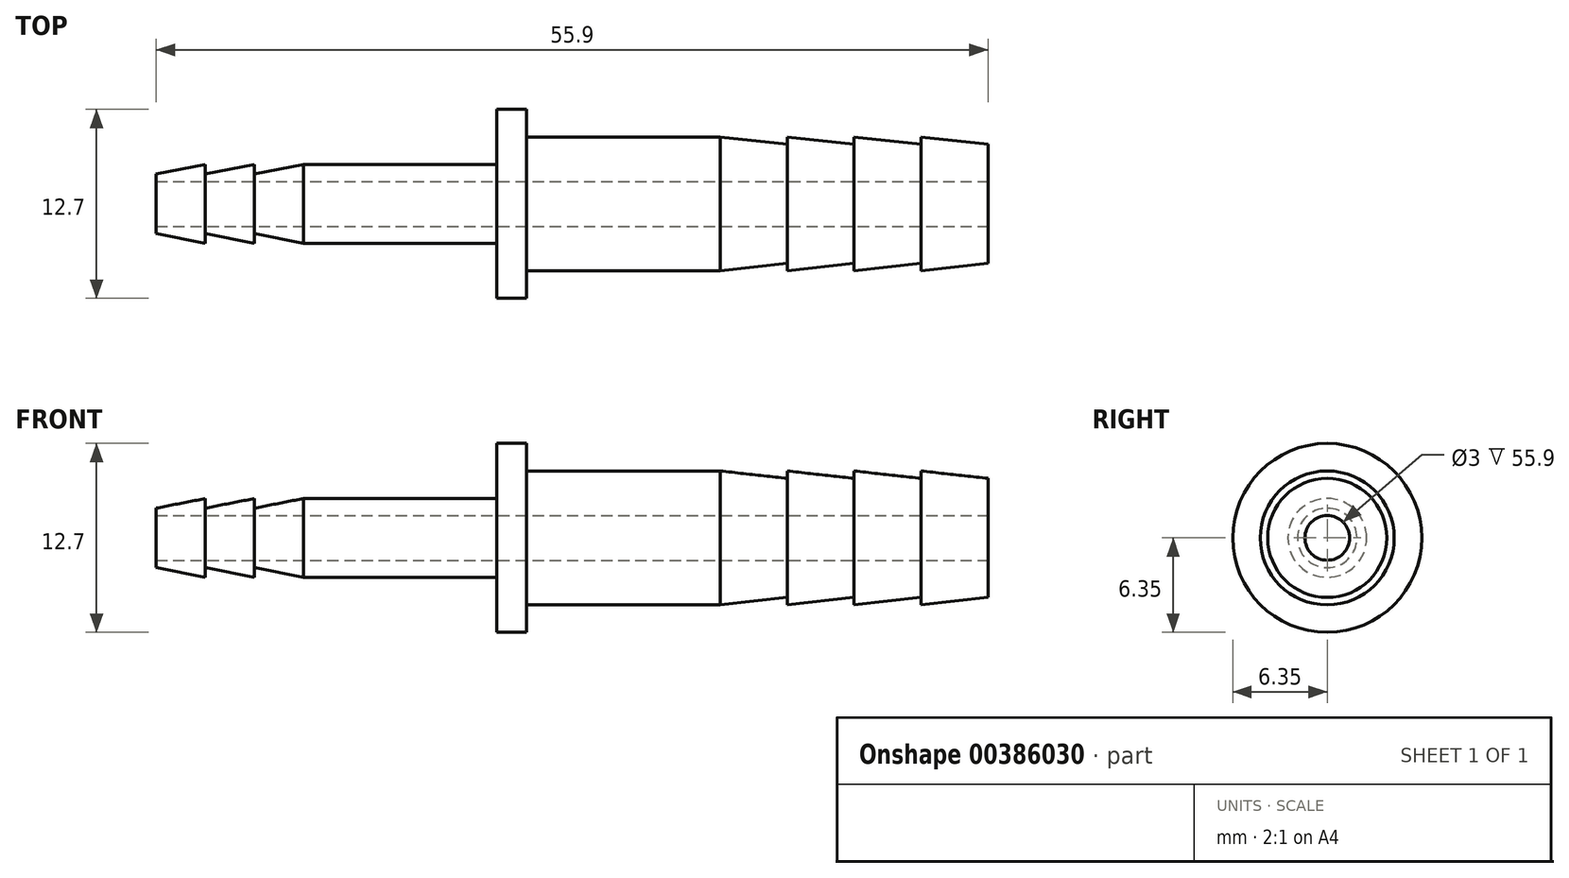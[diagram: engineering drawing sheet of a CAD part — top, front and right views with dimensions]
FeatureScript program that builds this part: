
annotation { "Feature Type Name" : "Feature", "Feature Type Description" : "" }
export const myFeature = defineFeature(function(context is Context, id is Id, definition is map)
    precondition{}
    {
        {
            var Q0;
            Q0=qCreatedBy(makeId("Front.planeOp"),FACE);
            var sketch = newSketch(context, id + "F0", { "sketchPlane" : qUnion([Q0])});
            skLineSegment(sketch, "E0.bottom", {"start": v(14, 4.5) * mm, "end": v(1, 4.5) * mm});
            skLineSegment(sketch, "E1", {"start": v(18.5, 4) * mm, "end": v(14, 4.5) * mm});
            skLineSegment(sketch, "E2", {"start": v(23, 4) * mm, "end": v(18.5, 4.5) * mm});
            skLineSegment(sketch, "E3", {"start": v(27.5, 4) * mm, "end": v(23, 4.5) * mm});
            skLineSegment(sketch, "E4.top", {"start": v(-14, 2.65) * mm, "end": v(-1, 2.65) * mm});
            skLineSegment(sketch, "E5", {"start": v(-17.3, 0) * mm, "end": v(-17.3, 2) * mm});
            skLineSegment(sketch, "E6", {"start": v(-17.3, 2) * mm, "end": v(-14, 2.65) * mm});
            skLineSegment(sketch, "E7", {"start": v(-20.6, 0) * mm, "end": v(-20.6, 2) * mm});
            skLineSegment(sketch, "E8", {"start": v(-20.6, 2) * mm, "end": v(-17.3, 2.65) * mm});
            skLineSegment(sketch, "E9", {"start": v(-23.9, 0) * mm, "end": v(-23.9, 2) * mm});
            skLineSegment(sketch, "E10", {"start": v(-23.9, 2) * mm, "end": v(-20.6, 2.65) * mm});
            skLineSegment(sketch, "E11", {"start": v(32, 4) * mm, "end": v(27.5, 4.5) * mm});
            skLineSegment(sketch, "E12.trimOffspring", {"start": v(-17.3, 2) * mm, "end": v(-17.3, 2.65) * mm});
            skLineSegment(sketch, "E13.trimOffspring", {"start": v(-20.6, 2) * mm, "end": v(-20.6, 2.65) * mm});
            skLineSegment(sketch, "E14", {"start": v(23, 4.5) * mm, "end": v(23, 4) * mm});
            skLineSegment(sketch, "E15", {"start": v(32, 4) * mm, "end": v(32, 0) * mm});
            skLineSegment(sketch, "E16", {"start": v(-23.9, 0) * mm, "end": v(32, 0) * mm});
            skLineSegment(sketch, "E17.bottom", {"start": v(1, 6.35) * mm, "end": v(-1, 6.35) * mm});
            skLineSegment(sketch, "E17.left", {"start": v(1, 6.35) * mm, "end": v(1, 4.5) * mm});
            skLineSegment(sketch, "E17.right", {"start": v(-1, 6.35) * mm, "end": v(-1, 2.65) * mm});
            skPoint(sketch, "E17.middle", {"position": v(0, 0) * mm});
            skLineSegment(sketch, "E18", {"start": v(27.5, 4) * mm, "end": v(27.5, 4.5) * mm});
            skLineSegment(sketch, "E19", {"start": v(18.5, 4) * mm, "end": v(18.5, 4.5) * mm});
            skLineSegment(sketch, "E20", {"start": v(-12.64, 18.93) * mm, "end": v(-12.64, 14.43) * mm});
            skLineSegment(sketch, "E21.top", {"start": v(-17.64, 17.08) * mm, "end": v(-12.64, 17.08) * mm});
            skLineSegment(sketch, "E22", {"start": v(-20.94, 14.43) * mm, "end": v(-20.94, 16.43) * mm});
            skLineSegment(sketch, "E23", {"start": v(-20.94, 16.43) * mm, "end": v(-17.64, 17.08) * mm});
            skLineSegment(sketch, "E24", {"start": v(-24.24, 14.43) * mm, "end": v(-24.24, 16.43) * mm});
            skLineSegment(sketch, "E25", {"start": v(-24.24, 16.43) * mm, "end": v(-20.94, 17.08) * mm});
            skLineSegment(sketch, "E26", {"start": v(-27.54, 14.43) * mm, "end": v(-27.54, 16.43) * mm});
            skLineSegment(sketch, "E27", {"start": v(-27.54, 16.43) * mm, "end": v(-24.24, 17.08) * mm});
            skLineSegment(sketch, "E28.trimOffspring", {"start": v(-20.94, 16.43) * mm, "end": v(-20.94, 17.08) * mm});
            skLineSegment(sketch, "E29.trimOffspring", {"start": v(-24.24, 16.43) * mm, "end": v(-24.24, 17.08) * mm});
            skLineSegment(sketch, "E30.trimOffspring", {"start": v(-12.64, 14.43) * mm, "end": v(-12.64, 18.93) * mm});
            skPoint(sketch, "E31.middle", {"position": v(-12.64, 14.43) * mm});
            skPoint(sketch, "E17.top.end.orphan", {"position": v(-1, -6.35) * mm});
            skPoint(sketch, "E17.top.start.orphan", {"position": v(1, -6.35) * mm});
            skSolve(sketch);
        }
        {
            var Q0;
            {var subQ1=sQuery(id+"F0.wireOp",EDGE,"E5");Q0=makeQuery(id+"F0.imprint","IMPRINT",FACE,{"disambiguationData":[TD([[makeQuery(id+"F0.imprint","IMPRINT",EDGE,{"derivedFrom":subQ1}),1.0]])]});}
            var Q1;
            {var subQ1=sQuery(id+"F0.wireOp",EDGE,"E4.top");Q1=makeQuery(id+"F0.imprint","IMPRINT",FACE,{"disambiguationData":[TD([[makeQuery(id+"F0.imprint","IMPRINT",EDGE,{"derivedFrom":subQ1}),-1.0]])]});}
            var Q2;
            {var subQ1=sQuery(id+"F0.wireOp",EDGE,"E7");Q2=makeQuery(id+"F0.imprint","IMPRINT",FACE,{"disambiguationData":[TD([[makeQuery(id+"F0.imprint","IMPRINT",EDGE,{"derivedFrom":subQ1}),1.0]])]});}
            var Q3;
            {var subQ1=sQuery(id+"F0.wireOp",EDGE,"E0.bottom");Q3=makeQuery(id+"F0.imprint","IMPRINT",FACE,{"disambiguationData":[TD([[makeQuery(id+"F0.imprint","IMPRINT",EDGE,{"derivedFrom":subQ1}),1.0]])]});}
            var Q4;
            Q4=sQuery(id+"F0.wireOp",EDGE,"E16");
            revolve(context, id + "F1", {"entities" : qUnion([Q0, Q1, Q2, Q3]), "axis" : qUnion([Q4]), "revolveType" : RevolveType.FULL});
        }
        {
            var Q0;
            Q0=makeQuery(id+"F1.opRevolve","SWEPT_FACE",FACE,{"disambiguationData":[OSD([sQuery(id+"F0.wireOp",EDGE,"E15")])]});
            var sketch = newSketch(context, id + "F2", { "sketchPlane" : qUnion([Q0])});
            skCircle(sketch, "E32", {"center": v(0, 0) * mm, "radius": 1.5 * mm});
            skSolve(sketch);
        }
        {
            var Q0;
            Q0=makeQuery(id+"F2.imprint","IMPRINT",FACE,{"disambiguationData":[TD([[makeQuery(id+"F2.imprint","IMPRINT",EDGE,{"derivedFrom":sQuery(id+"F2.wireOp",EDGE,"E32")}),1.0]])]});
            extrude(context, id + "F3", {"entities" : qUnion([Q0]), "operationType" : NewBodyOperationType.REMOVE, "endBound" : BoundingType.THROUGH_ALL, "oppositeDirection" : true, "depth" : 25 * mm});
        }
    });
